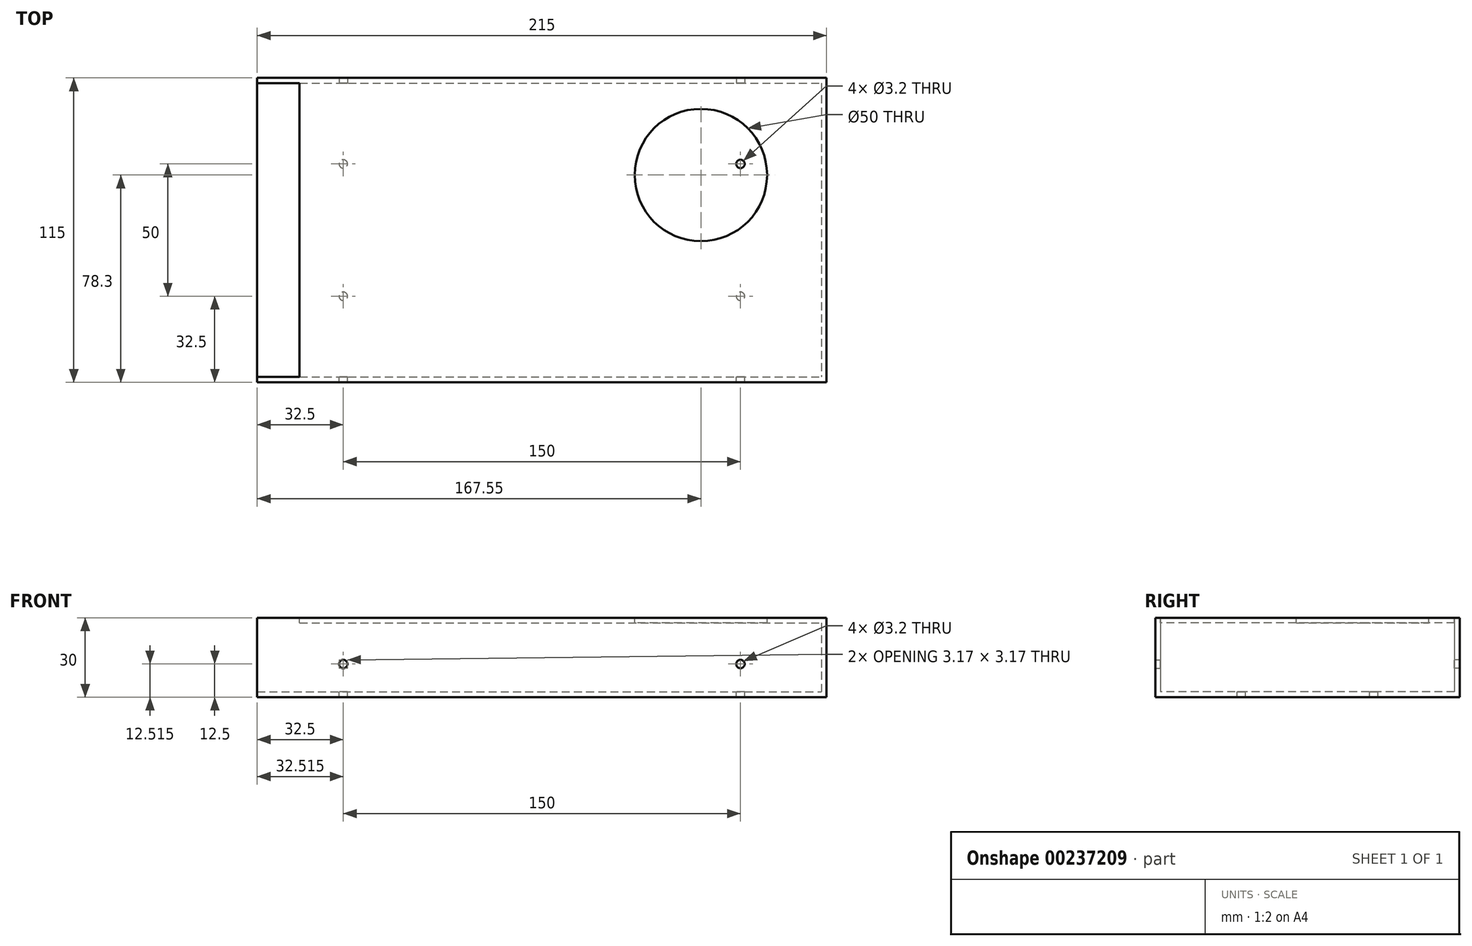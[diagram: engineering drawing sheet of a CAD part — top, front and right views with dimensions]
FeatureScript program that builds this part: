
annotation { "Feature Type Name" : "Feature", "Feature Type Description" : "" }
export const myFeature = defineFeature(function(context is Context, id is Id, definition is map)
    precondition{}
    {
        {
            var Q0;
            Q0=qCreatedBy(makeId("Top.planeOp"),FACE);
            var sketch = newSketch(context, id + "F0", { "sketchPlane" : qUnion([Q0])});
            skLineSegment(sketch, "E0.bottom", {"start": v(-107.5, 57.5) * mm, "end": v(107.5, 57.5) * mm});
            skLineSegment(sketch, "E0.top", {"start": v(-107.5, -57.5) * mm, "end": v(107.5, -57.5) * mm});
            skLineSegment(sketch, "E0.left", {"start": v(-107.5, 57.5) * mm, "end": v(-107.5, -57.5) * mm});
            skLineSegment(sketch, "E0.right", {"start": v(107.5, 57.5) * mm, "end": v(107.5, -57.5) * mm});
            skPoint(sketch, "E1", {"position": v(0, 57.5) * mm});
            skPoint(sketch, "E2", {"position": v(107.5, 0) * mm});
            skSolve(sketch);
        }
        {
            var Q0;
            Q0=makeQuery(id+"F0.imprint","IMPRINT",FACE,{"disambiguationData":[TD([[makeQuery(id+"F0.imprint","IMPRINT",EDGE,{"derivedFrom":sQuery(id+"F0.wireOp",EDGE,"E0.bottom")}),-1.0]])]});
            extrude(context, id + "F1", {"entities" : qUnion([Q0]), "depth" : 30 * mm});
        }
        {
            var Q0;
            Q0=makeQuery(id+"F1.opExtrude","CAP_FACE",FACE,{"disambiguationData":[OSD([sQuery(id+"F0.wireOp",EDGE,"E0.bottom"),sQuery(id+"F0.wireOp",EDGE,"E0.top"),sQuery(id+"F0.wireOp",EDGE,"E0.left"),sQuery(id+"F0.wireOp",EDGE,"E0.right")])],"isStart":false});
            var sketch = newSketch(context, id + "F2", { "sketchPlane" : qUnion([Q0])});
            skCircle(sketch, "E3", {"center": v(60.05, 20.8) * mm, "radius": 25 * mm});
            skSolve(sketch);
        }
        {
            var Q0;
            Q0=makeQuery(id+"F1.opExtrude","SWEPT_FACE",FACE,{"disambiguationData":[OSD([sQuery(id+"F0.wireOp",EDGE,"E0.left")])]});
            shell(context, id + "F3", {"entities" : qUnion([Q0]), "thickness" : 2 * mm});
        }
        {
            var Q0;
            Q0=makeQuery(id+"F2.imprint","IMPRINT",FACE,{"disambiguationData":[TD([[makeQuery(id+"F2.imprint","IMPRINT",EDGE,{"derivedFrom":sQuery(id+"F2.wireOp",EDGE,"E3")}),-1.0]])]});
            var sketch = newSketch(context, id + "F4", { "sketchPlane" : qUnion([Q0])});
            skLineSegment(sketch, "E4.bottom", {"start": v(-107.5, 55.5) * mm, "end": v(-91.5, 55.5) * mm});
            skLineSegment(sketch, "E4.top", {"start": v(-107.5, -55.5) * mm, "end": v(-91.5, -55.5) * mm});
            skLineSegment(sketch, "E4.left", {"start": v(-107.5, 55.5) * mm, "end": v(-107.5, -55.5) * mm});
            skLineSegment(sketch, "E4.right", {"start": v(-91.5, 55.5) * mm, "end": v(-91.5, -55.5) * mm});
            skSolve(sketch);
        }
        {
            var Q0;
            Q0=makeQuery(id+"F4.imprint","IMPRINT",FACE,{"disambiguationData":[TD([[makeQuery(id+"F4.imprint","IMPRINT",EDGE,{"derivedFrom":sQuery(id+"F4.wireOp",EDGE,"E4.bottom")}),-1.0]])]});
            var Q1;
            Q1=makeQuery(id+"F2.imprint","IMPRINT",FACE,{"disambiguationData":[TD([[makeQuery(id+"F2.imprint","IMPRINT",EDGE,{"derivedFrom":sQuery(id+"F2.wireOp",EDGE,"E3")}),1.0]])]});
            extrude(context, id + "F5", {"entities" : qUnion([Q0, Q1]), "operationType" : NewBodyOperationType.REMOVE, "endBound" : BoundingType.UP_TO_NEXT, "oppositeDirection" : true, "depth" : 25 * mm});
        }
        {
            var Q0;
            Q0=makeQuery(id+"F1.opExtrude","CAP_FACE",FACE,{"disambiguationData":[OSD([sQuery(id+"F0.wireOp",EDGE,"E0.bottom"),sQuery(id+"F0.wireOp",EDGE,"E0.top"),sQuery(id+"F0.wireOp",EDGE,"E0.left"),sQuery(id+"F0.wireOp",EDGE,"E0.right")])],"isStart":true});
            var sketch = newSketch(context, id + "F6", { "sketchPlane" : qUnion([Q0])});
            skPoint(sketch, "E5", {"position": v(75, 25) * mm});
            skPoint(sketch, "E6", {"position": v(-75, 25) * mm});
            skPoint(sketch, "E7", {"position": v(-75, -25) * mm});
            skPoint(sketch, "E8", {"position": v(75, -25) * mm});
            skSolve(sketch);
        }
        {
            var Q0;
            Q0=makeQuery(id+"F1.opExtrude","SWEPT_FACE",FACE,{"disambiguationData":[OSD([sQuery(id+"F0.wireOp",EDGE,"E0.top")])]});
            var sketch = newSketch(context, id + "F7", { "sketchPlane" : qUnion([Q0])});
            skPoint(sketch, "E9", {"position": v(-75, 12.5) * mm});
            skPoint(sketch, "E10", {"position": v(75, 12.5) * mm});
            skSolve(sketch);
        }
        {
            var Q0;
            Q0=makeQuery(id+"F1.opExtrude","SWEPT_FACE",FACE,{"disambiguationData":[OSD([sQuery(id+"F0.wireOp",EDGE,"E0.bottom")])]});
            var sketch = newSketch(context, id + "F8", { "sketchPlane" : qUnion([Q0])});
            skPoint(sketch, "E11", {"position": v(-75, 12.5) * mm});
            skPoint(sketch, "E12", {"position": v(75, 12.5) * mm});
            skSolve(sketch);
        }
        {
            var Q0;
            Q0=sQuery(id+"F6.wireOp",VERTEX,"E6");
            var Q1;
            Q1=sQuery(id+"F6.wireOp",VERTEX,"E8");
            var Q2;
            Q2=sQuery(id+"F6.wireOp",VERTEX,"E7");
            var Q3;
            Q3=sQuery(id+"F6.wireOp",VERTEX,"E5");
            var Q4;
            Q4=sQuery(id+"F7.wireOp",VERTEX,"E9");
            var Q5;
            Q5=sQuery(id+"F7.wireOp",VERTEX,"E10");
            var Q6;
            Q6=sQuery(id+"F8.wireOp",VERTEX,"E11");
            var Q7;
            Q7=sQuery(id+"F8.wireOp",VERTEX,"E12");
            var Q8;
            Q8=makeQuery(id+"F1.opExtrude","SWEPT_BODY",BODY,{"disambiguationData":[OSD([sQuery(id+"F0.wireOp",EDGE,"E0.bottom"),sQuery(id+"F0.wireOp",EDGE,"E0.top"),sQuery(id+"F0.wireOp",EDGE,"E0.left"),sQuery(id+"F0.wireOp",EDGE,"E0.right")])]});
            hole(context, id + "F9", {"style" : HoleStyle.SIMPLE, "endStyle" : HoleEndStyle.BLIND, "standardTappedOrClearance" : lookupTablePath({ "standard" : "ISO", "engagement" : "75%", "pitch" : "0.75 mm", "size" : "M4", "type" : "Tapped" }), "standardBlindInLast" : lookupTablePath({ "standard" : "ISO", "engagement" : "75%", "pitch" : "0.75 mm", "size" : "M4", "type" : "Tapped" }), "holeDiameter" : 3.2 * mm, "holeDepth" : 5 * mm, "startFromSketch" : true, "locations" : qUnion([Q0, Q1, Q2, Q3, Q4, Q5, Q6, Q7]), "scope" : qUnion([Q8])});
        }
    });
